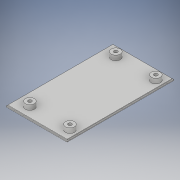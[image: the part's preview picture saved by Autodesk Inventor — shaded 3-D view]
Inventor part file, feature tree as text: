
AUTODESK INVENTOR PART (.ipt)
format: ipt  version: 2019 (Build 230136000, 136)  size: 167,424 bytes
history: native  units: mm
features: extrude x5, sketch x5
ambient origin geometry x8: Origin, YZ Plane, XZ Plane, XY Plane, X Axis, Y Axis, Z Axis, Center Point
bodies: Volumenkörper1 (feature_tree)
feature tree (10):
  extrude  "Extrusion1"  Depth=54.1mm
  extrude  "Extrusion2"  Depth=0.75mm
  extrude  "Extrusion3"  Depth=0.75mm
  extrude  "Extrusion4"  Depth=8.0mm
  extrude  "Extrusion5"  Depth=3.5mm
  sketch  "Skizze1"  dims[d0=94.74mm d1=54.1mm]
  sketch  "Skizze2"  dims[d2=1.5mm d3=0.0mm d4=0.75mm]
  sketch  "Skizze3"  dims[d5=0.75mm d6=0.0mm d7=8.0mm]
  sketch  "Skizze4"  dims[d8=8.0mm d9=8.0mm]
  sketch  "Skizze5"  dims[d10=8.0mm d12=5.98mm d13=5.98mm d14=35.56mm d15=35.56mm d16=8.52mm d17=76.2mm d18=4.25mm d19=0.0mm d20=3.1mm d21=3.1mm d22=3.1mm d23=3.1mm d24=10.0mm d25=0.0mm d26=6.0mm d27=6.0mm d28=6.0mm d29=6.0mm d30=3.5mm d31=0.0mm]
